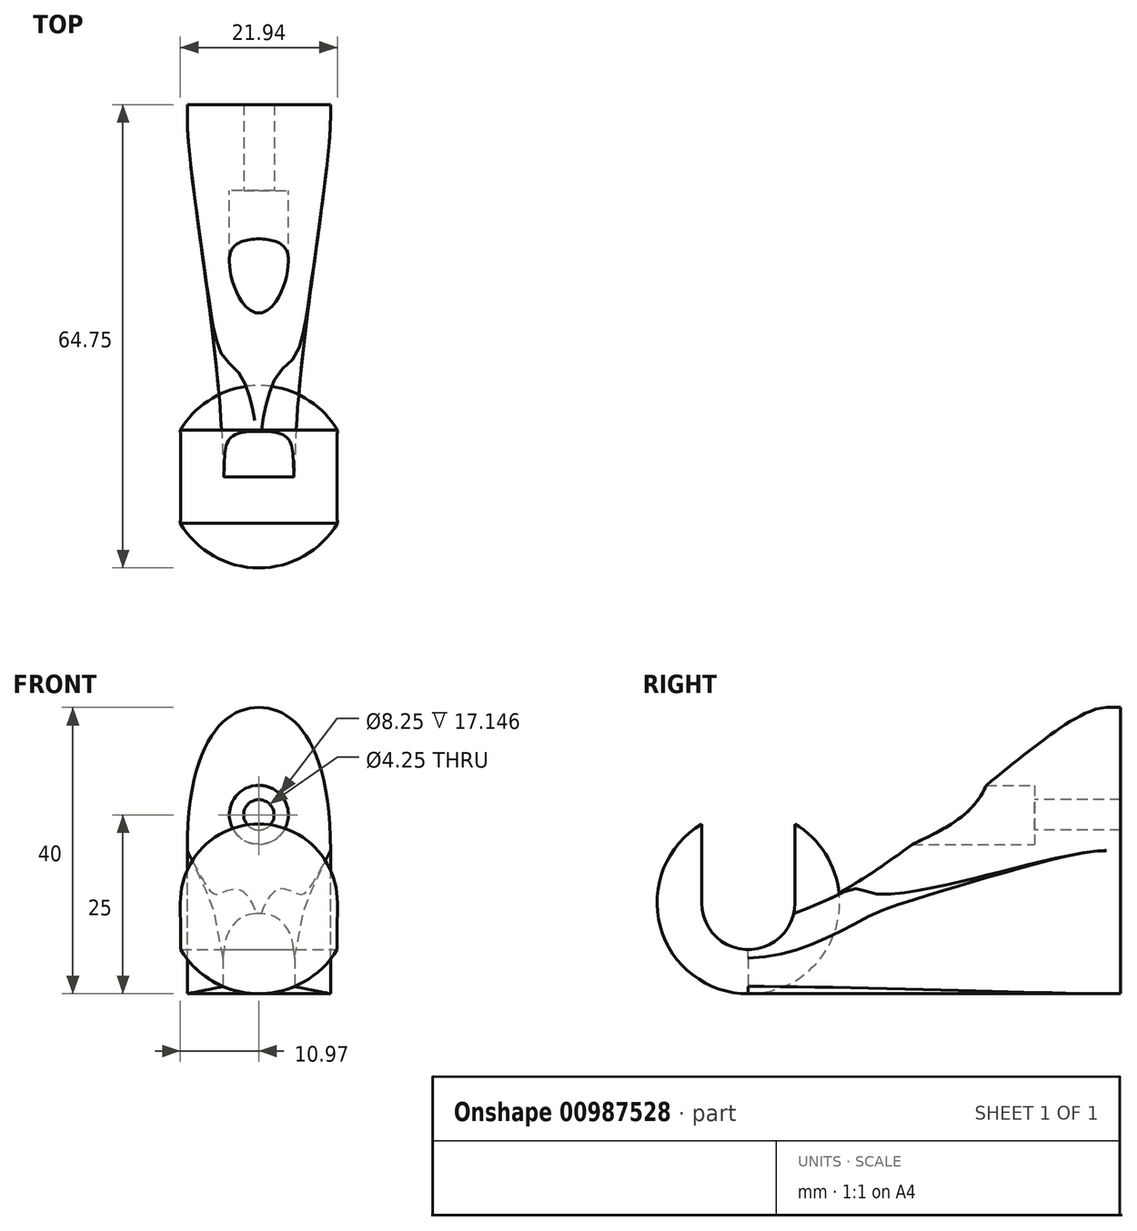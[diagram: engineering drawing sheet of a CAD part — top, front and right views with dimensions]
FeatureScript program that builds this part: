
annotation { "Feature Type Name" : "Feature", "Feature Type Description" : "" }
export const myFeature = defineFeature(function(context is Context, id is Id, definition is map)
    precondition{}
    {
        {
            var Q0;
            Q0=qCreatedBy(makeId("Right.planeOp"),FACE);
            var sketch = newSketch(context, id + "F0", { "sketchPlane" : qUnion([Q0])});
            skPoint(sketch, "E0.middle", {"position": v(0, 7.66) * mm});
            skPoint(sketch, "E1", {"position": v(-6.5, 7.66) * mm});
            skPoint(sketch, "E2", {"position": v(6.5, 7.66) * mm});
            skLineSegment(sketch, "E3.bottom", {"start": v(-6.5, 7.66) * mm, "end": v(6.5, 7.66) * mm, "construction": true});
            skLineSegment(sketch, "E3.top", {"start": v(-6.5, 23.44) * mm, "end": v(6.5, 23.44) * mm});
            skLineSegment(sketch, "E3.left", {"start": v(-6.5, 7.66) * mm, "end": v(-6.5, 23.44) * mm});
            skLineSegment(sketch, "E3.right", {"start": v(6.5, 7.66) * mm, "end": v(6.5, 23.44) * mm});
            skArc(sketch, "E4", {"start": v(-6.5, 7.66) * mm, "mid": v(0, 1.16) * mm, "end": v(6.5, 7.66) * mm});
            skArc(sketch, "E5", {"start": v(6.5, 7.66) * mm, "mid": v(0, 14.16) * mm, "end": v(-6.5, 7.66) * mm, "construction": true});
            skSolve(sketch);
        }
        {
            var Q0;
            Q0=qCreatedBy(makeId("Front.planeOp"),FACE);
            cPlane(context, id + "F1", {"entities" : qUnion([Q0]), "cplaneType" : CPlaneType.OFFSET, "offset" : 50 * mm, "oppositeDirection" : true, "width" : 150 * mm, "height" : 150 * mm});
        }
        {
            var Q0;
            Q0=qCreatedBy(makeId("Front.planeOp"),FACE);
            var sketch = newSketch(context, id + "F2", { "sketchPlane" : qUnion([Q0])});
            skLineSegment(sketch, "E6.bottom", {"start": v(-5, 5) * mm, "end": v(5, 5) * mm});
            skLineSegment(sketch, "E6.top", {"start": v(-5, -5) * mm, "end": v(5, -5) * mm});
            skLineSegment(sketch, "E6.left", {"start": v(-5, 5) * mm, "end": v(-5, -5) * mm});
            skLineSegment(sketch, "E6.right", {"start": v(5, 5) * mm, "end": v(5, -5) * mm});
            skPoint(sketch, "E6.middle", {"position": v(0, 0) * mm});
            skPoint(sketch, "E7", {"position": v(0, 5) * mm});
            skArc(sketch, "E8", {"start": v(0, 20.5) * mm, "mid": v(12.75, 7.75) * mm, "end": v(0, -5) * mm});
            skLineSegment(sketch, "E9", {"start": v(0, 20.5) * mm, "end": v(0, -5) * mm});
            skArc(sketch, "E10.MirrorCS", {"start": v(0, 20.5) * mm, "mid": v(-12.75, 7.75) * mm, "end": v(0, -5) * mm});
            skSolve(sketch);
        }
        {
            var Q0;
            Q0=qCreatedBy(id+"F1.planeOp",FACE);
            var sketch = newSketch(context, id + "F3", { "sketchPlane" : qUnion([Q0])});
            skLineSegment(sketch, "E11.bottom", {"start": v(-10, -5) * mm, "end": v(0, -5) * mm});
            skLineSegment(sketch, "E11.top", {"start": v(-10, 35) * mm, "end": v(10, 35) * mm});
            skLineSegment(sketch, "E11.left", {"start": v(-10, -5) * mm, "end": v(-10, 35) * mm});
            skLineSegment(sketch, "E11.right", {"start": v(10, -5) * mm, "end": v(10, 35) * mm});
            skFitSpline(sketch, "E12", {"points": [v(-10, 15) * mm, v(0, 35) * mm, v(10, 15) * mm], "startDerivative": vector(0, 90) * mm, "endDerivative": vector(0, -90) * mm});
            skLineSegment(sketch, "E13", {"start": v(0, -5) * mm, "end": v(10, -5) * mm});
            skLineSegment(sketch, "E14", {"start": v(0, 35) * mm, "end": v(0, -5) * mm, "construction": true});
            skPoint(sketch, "E15", {"position": v(0, 18.53) * mm});
            skSolve(sketch);
        }
        {
            var Q0;
            {var subQ4=sQuery(id+"F3.wireOp",EDGE,"E11.bottom");Q0=makeQuery(id+"F3.imprint","IMPRINT",FACE,{"disambiguationData":[TD([[makeQuery(id+"F3.imprint","IMPRINT",EDGE,{"derivedFrom":subQ4}),1.0]])]});}
            var Q1;
            Q1=makeQuery(id+"F2.imprint","IMPRINT",FACE,{"disambiguationData":[TD([[makeQuery(id+"F2.imprint","IMPRINT",EDGE,{"derivedFrom":sQuery(id+"F2.wireOp",EDGE,"E6.bottom")}),-1.0]])]});
            var Q2;
            Q2=sQuery(id+"F3.wireOp",VERTEX,"E12.1.internal");
            var Q3;
            Q3=sQuery(id+"F2.wireOp",VERTEX,"E7");
            loft(context, id + "F4", {"startCondition" : LoftEndDerivativeType.NORMAL_TO_PROFILE, "startMagnitude" : .5, "endCondition" : LoftEndDerivativeType.NORMAL_TO_PROFILE, "endMagnitude" : 1, "sheetProfilesArray" : [{ "sheetProfileEntities" : qUnion([Q0]) }, { "sheetProfileEntities" : qUnion([Q1]) }], "matchConnections" : true, "connections" : [{ "connectionEntities" : qUnion([Q2, Q3]), "connectionEdgeQueries" : qUnion([]), "connectionEdgeParameters" : [] }]});
        }
        {
            var Q0;
            {var subQ4=sQuery(id+"F3.wireOp",EDGE,"E11.bottom");Q0=makeQuery(id+"F3.imprint","IMPRINT",FACE,{"disambiguationData":[TD([[makeQuery(id+"F3.imprint","IMPRINT",EDGE,{"derivedFrom":subQ4}),1.0]])]});}
            extrude(context, id + "F5", {"entities" : qUnion([Q0]), "operationType" : NewBodyOperationType.ADD, "oppositeDirection" : true, "depth" : 2 * mm, "offsetDistance" : 25 * mm});
        }
        {
            var Q0;
            {var subQ0=sQuery(id+"F2.wireOp",EDGE,"E6.right");var subQ1=sQuery(id+"F2.wireOp",EDGE,"E6.bottom");var subQ2=makeQuery(id+"F2.imprint","INTERSECT",VERTEX,{"derivedFrom":[subQ1,subQ0]});Q0=makeQuery(id+"F2.imprint","IMPRINT",FACE,{"disambiguationData":[TD([[makeQuery(id+"F2.imprint","IMPRINT",EDGE,{"disambiguationData":[TD([[subQ2,1.0]])],"derivedFrom":subQ1}),1.0]])]});}
            var Q1;
            {var subQ0=sQuery(id+"F2.wireOp",EDGE,"E6.right");var subQ1=sQuery(id+"F2.wireOp",EDGE,"E6.bottom");var subQ2=makeQuery(id+"F2.imprint","INTERSECT",VERTEX,{"derivedFrom":[subQ1,subQ0]});Q1=makeQuery(id+"F2.imprint","IMPRINT",FACE,{"disambiguationData":[TD([[makeQuery(id+"F2.imprint","IMPRINT",EDGE,{"disambiguationData":[TD([[subQ2,1.0]])],"derivedFrom":subQ1}),-1.0]])]});}
            var Q2;
            Q2=sQuery(id+"F2.wireOp",EDGE,"E9");
            revolve(context, id + "F6", {"surfaceOperationType" : NewSurfaceOperationType.NEW, "entities" : qUnion([Q0, Q1]), "axis" : qUnion([Q2]), "revolveType" : RevolveType.FULL});
        }
        {
            var Q0;
            Q0=makeQuery(id+"F0.imprint","IMPRINT",FACE,{"disambiguationData":[TD([[makeQuery(id+"F0.imprint","IMPRINT",EDGE,{"derivedFrom":sQuery(id+"F0.wireOp",EDGE,"E3.top")}),-1.0]])]});
            extrude(context, id + "F7", {"entities" : qUnion([Q0]), "operationType" : NewBodyOperationType.REMOVE, "endBound" : BoundingType.SYMMETRIC, "oppositeDirection" : true, "depth" : 30 * mm, "offsetDistance" : 25 * mm});
        }
        {
            var Q0;
            {var subQ4=sQuery(id+"F3.wireOp",EDGE,"E11.bottom");Q0=makeQuery(id+"F3.imprint","IMPRINT",FACE,{"disambiguationData":[TD([[makeQuery(id+"F3.imprint","IMPRINT",EDGE,{"derivedFrom":subQ4}),1.0]])]});}
            cPlane(context, id + "F8", {"entities" : qUnion([Q0]), "cplaneType" : CPlaneType.OFFSET, "offset" : 10 * mm, "width" : 150 * mm, "height" : 150 * mm});
        }
        {
            var Q0;
            Q0=qCreatedBy(id+"F8.planeOp",FACE);
            var sketch = newSketch(context, id + "F9", { "sketchPlane" : qUnion([Q0])});
            skCircle(sketch, "E16", {"center": v(0, 20) * mm, "radius": 2.12 * mm});
            skCircle(sketch, "E17", {"center": v(0, 20) * mm, "radius": 4.12 * mm});
            skSolve(sketch);
        }
        {
            var Q0;
            Q0=makeQuery(id+"F9.imprint","IMPRINT",FACE,{"disambiguationData":[TD([[makeQuery(id+"F9.imprint","IMPRINT",EDGE,{"derivedFrom":sQuery(id+"F9.wireOp",EDGE,"E16")}),1.0]])]});
            var Q1;
            Q1=makeQuery(id+"F9.imprint","IMPRINT",FACE,{"disambiguationData":[TD([[makeQuery(id+"F9.imprint","IMPRINT",EDGE,{"derivedFrom":sQuery(id+"F9.wireOp",EDGE,"E16")}),-1.0]])]});
            extrude(context, id + "F10", {"entities" : qUnion([Q0, Q1]), "operationType" : NewBodyOperationType.REMOVE, "depth" : 20 * mm, "offsetDistance" : 25 * mm});
        }
        {
            var Q0;
            Q0=makeQuery(id+"F9.imprint","IMPRINT",FACE,{"disambiguationData":[TD([[makeQuery(id+"F9.imprint","IMPRINT",EDGE,{"derivedFrom":sQuery(id+"F9.wireOp",EDGE,"E16")}),1.0]])]});
            extrude(context, id + "F11", {"entities" : qUnion([Q0]), "operationType" : NewBodyOperationType.REMOVE, "oppositeDirection" : true, "depth" : 15 * mm, "offsetDistance" : 25 * mm});
        }
        {
            var Q0;
            Q0=makeQuery(id+"F4.opLoft","SWEPT_EDGE",EDGE,{"disambiguationData":[OSD([sQuery(id+"F2.wireOp",EDGE,"E6.bottom"),sQuery(id+"F2.wireOp",EDGE,"E6.left"),sQuery(id+"F3.wireOp",EDGE,"E11.left"),sQuery(id+"F3.wireOp",EDGE,"E12")])]});
            var Q1;
            Q1=makeQuery(id+"F4.opLoft","SWEPT_EDGE",EDGE,{"disambiguationData":[OSD([sQuery(id+"F2.wireOp",EDGE,"E6.bottom"),sQuery(id+"F2.wireOp",EDGE,"E6.right"),sQuery(id+"F3.wireOp",EDGE,"E11.right"),sQuery(id+"F3.wireOp",EDGE,"E12")])]});
            fillet(context, id + "F12", {"entities" : qUnion([Q0, Q1]), "radius" : 5 * mm, "tangentPropagation" : true, "allowEdgeOverflow" : false});
        }
    });
